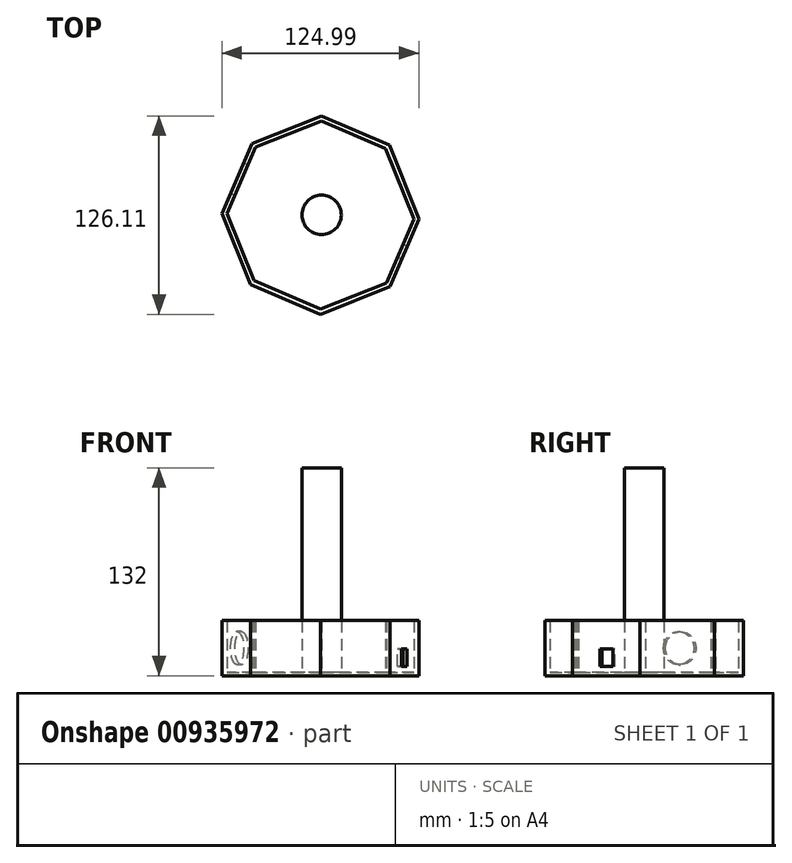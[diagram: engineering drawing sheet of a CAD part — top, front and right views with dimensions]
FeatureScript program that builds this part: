
annotation { "Feature Type Name" : "Feature", "Feature Type Description" : "" }
export const myFeature = defineFeature(function(context is Context, id is Id, definition is map)
    precondition{}
    {
        {
            var Q0;
            Q0=qCreatedBy(makeId("Top.planeOp"),FACE);
            var sketch = newSketch(context, id + "F0", { "sketchPlane" : qUnion([Q0])});
            skCircle(sketch, "E0.cCircle", {"center": v(0, 0) * mm, "radius": 60 * mm, "construction": true});
            skLineSegment(sketch, "E1.0", {"start": v(-44.1, 45.28) * mm, "end": v(0.06, 62.9) * mm});
            skLineSegment(sketch, "E1.1", {"start": v(0.06, 62.9) * mm, "end": v(42.99, 44.45) * mm});
            skLineSegment(sketch, "E1.2", {"start": v(42.99, 44.45) * mm, "end": v(61.78, -2.66) * mm});
            skLineSegment(sketch, "E1.3", {"start": v(61.78, -2.66) * mm, "end": v(43.34, -45.59) * mm});
            skLineSegment(sketch, "E1.4", {"start": v(43.34, -45.59) * mm, "end": v(-0.83, -63.2) * mm});
            skLineSegment(sketch, "E1.5", {"start": v(-0.83, -63.2) * mm, "end": v(-45.28, -44.1) * mm});
            skLineSegment(sketch, "E1.6", {"start": v(-45.28, -44.1) * mm, "end": v(-63.2, 0.83) * mm});
            skLineSegment(sketch, "E1.7", {"start": v(-63.2, 0.83) * mm, "end": v(-44.1, 45.28) * mm});
            skPoint(sketch, "E1.0.midPoint", {"position": v(-21.64, 54.24) * mm});
            skLineSegment(sketch, "E2.0", {"start": v(-59.96, 0.79) * mm, "end": v(-41.84, 42.96) * mm});
            skLineSegment(sketch, "E2.1", {"start": v(-42.96, -41.84) * mm, "end": v(-59.96, 0.79) * mm});
            skLineSegment(sketch, "E2.2", {"start": v(-41.84, 42.96) * mm, "end": v(0.02, 59.65) * mm});
            skLineSegment(sketch, "E2.3", {"start": v(-0.79, -59.96) * mm, "end": v(-42.96, -41.84) * mm});
            skLineSegment(sketch, "E2.4", {"start": v(0.02, 59.65) * mm, "end": v(40.66, 42.19) * mm});
            skLineSegment(sketch, "E2.5", {"start": v(40.66, 42.19) * mm, "end": v(58.54, -2.62) * mm});
            skLineSegment(sketch, "E2.6", {"start": v(58.54, -2.62) * mm, "end": v(41.07, -43.26) * mm});
            skLineSegment(sketch, "E2.7", {"start": v(41.07, -43.26) * mm, "end": v(-0.79, -59.96) * mm});
            skSolve(sketch);
        }
        {
            var Q0;
            Q0=makeQuery(id+"F0.imprint","IMPRINT",FACE,{"disambiguationData":[TD([[makeQuery(id+"F0.imprint","IMPRINT",EDGE,{"derivedFrom":sQuery(id+"F0.wireOp",EDGE,"E1.0")}),-1.0]])]});
            extrude(context, id + "F1", {"entities" : qUnion([Q0]), "depth" : 35 * mm, "offsetDistance" : 25 * mm});
        }
        {
            var Q0;
            Q0=makeQuery(id+"F0.imprint","IMPRINT",FACE,{"disambiguationData":[TD([[makeQuery(id+"F0.imprint","IMPRINT",EDGE,{"derivedFrom":sQuery(id+"F0.wireOp",EDGE,"E2.0")}),-1.0]])]});
            extrude(context, id + "F2", {"entities" : qUnion([Q0]), "operationType" : NewBodyOperationType.ADD, "depth" : 2 * mm, "offsetDistance" : 25 * mm});
        }
        {
            var Q0;
            Q0=makeQuery(id+"F1.opExtrude","SWEPT_FACE",FACE,{"disambiguationData":[OSD([sQuery(id+"F0.wireOp",EDGE,"E1.3")])]});
            var sketch = newSketch(context, id + "F3", { "sketchPlane" : qUnion([Q0])});
            skLineSegment(sketch, "E3.0.0", {"start": v(-24.78, 0) * mm, "end": v(21.95, 0) * mm});
            skLineSegment(sketch, "E3.0.1", {"start": v(21.95, 0) * mm, "end": v(21.95, 35) * mm});
            skLineSegment(sketch, "E3.0.2", {"start": v(21.95, 35) * mm, "end": v(-24.78, 35) * mm});
            skLineSegment(sketch, "E3.0.3", {"start": v(-24.78, 35) * mm, "end": v(-24.78, 0) * mm});
            skLineSegment(sketch, "E4", {"start": v(-24.78, 35) * mm, "end": v(21.95, 0) * mm, "construction": true});
            skLineSegment(sketch, "E5.bottom", {"start": v(-5.76, 17) * mm, "end": v(3.24, 17) * mm});
            skLineSegment(sketch, "E5.top", {"start": v(-5.76, 6) * mm, "end": v(3.24, 6) * mm});
            skLineSegment(sketch, "E5.left", {"start": v(-5.76, 17) * mm, "end": v(-5.76, 6) * mm});
            skLineSegment(sketch, "E5.right", {"start": v(3.24, 17) * mm, "end": v(3.24, 6) * mm});
            skPoint(sketch, "E5.middle", {"position": v(-1.41, 17.5) * mm});
            skLineSegment(sketch, "E6", {"start": v(-1.41, 35) * mm, "end": v(-1.41, 0) * mm, "construction": true});
            skSolve(sketch);
        }
        {
            var Q0;
            Q0=makeQuery(id+"F3.imprint","IMPRINT",FACE,{"disambiguationData":[TD([[makeQuery(id+"F3.imprint","IMPRINT",EDGE,{"derivedFrom":sQuery(id+"F3.wireOp",EDGE,"E5.bottom")}),-1.0]])]});
            var Q1;
            Q1=makeQuery(id+"F1.opExtrude","SWEPT_FACE",FACE,{"disambiguationData":[OSD([sQuery(id+"F0.wireOp",EDGE,"E2.6")])]});
            extrude(context, id + "F4", {"entities" : qUnion([Q0]), "operationType" : NewBodyOperationType.REMOVE, "endBound" : BoundingType.UP_TO_SURFACE, "oppositeDirection" : true, "depth" : 5 * mm, "endBoundEntityFace" : qUnion([Q1]), "offsetDistance" : 25 * mm});
        }
        {
            var Q0;
            Q0=makeQuery(id+"F2.opExtrude","CAP_FACE",FACE,{"disambiguationData":[OSD([sQuery(id+"F0.wireOp",EDGE,"E2.0"),sQuery(id+"F0.wireOp",EDGE,"E2.1"),sQuery(id+"F0.wireOp",EDGE,"E2.2"),sQuery(id+"F0.wireOp",EDGE,"E2.3"),sQuery(id+"F0.wireOp",EDGE,"E2.4"),sQuery(id+"F0.wireOp",EDGE,"E2.5"),sQuery(id+"F0.wireOp",EDGE,"E2.6"),sQuery(id+"F0.wireOp",EDGE,"E2.7")])],"isStart":false});
            var sketch = newSketch(context, id + "F5", { "sketchPlane" : qUnion([Q0])});
            skCircle(sketch, "E7", {"center": v(0, 0) * mm, "radius": 12.5 * mm});
            skSolve(sketch);
        }
        {
            var Q0;
            Q0=makeQuery(id+"F5.imprint","IMPRINT",FACE,{"disambiguationData":[TD([[makeQuery(id+"F5.imprint","IMPRINT",EDGE,{"derivedFrom":sQuery(id+"F5.wireOp",EDGE,"E7")}),1.0]])]});
            extrude(context, id + "F6", {"entities" : qUnion([Q0]), "operationType" : NewBodyOperationType.ADD, "depth" : 130 * mm, "offsetDistance" : 25 * mm});
        }
        {
            var Q0;
            Q0=makeQuery(id+"F1.opExtrude","SWEPT_FACE",FACE,{"disambiguationData":[OSD([sQuery(id+"F0.wireOp",EDGE,"E1.7")])]});
            var sketch = newSketch(context, id + "F7", { "sketchPlane" : qUnion([Q0])});
            skLineSegment(sketch, "E8", {"start": v(-24.2, 35) * mm, "end": v(24.2, 0) * mm, "construction": true});
            skCircle(sketch, "E9", {"center": v(0, 17.5) * mm, "radius": 10.5 * mm});
            skSolve(sketch);
        }
        {
            var Q0;
            Q0=makeQuery(id+"F7.imprint","IMPRINT",FACE,{"disambiguationData":[TD([[makeQuery(id+"F7.imprint","IMPRINT",EDGE,{"derivedFrom":sQuery(id+"F7.wireOp",EDGE,"E9")}),1.0]])]});
            var Q1;
            Q1=makeQuery(id+"F1.opExtrude","SWEPT_FACE",FACE,{"disambiguationData":[OSD([sQuery(id+"F0.wireOp",EDGE,"E2.0")])]});
            extrude(context, id + "F8", {"entities" : qUnion([Q0]), "operationType" : NewBodyOperationType.REMOVE, "endBound" : BoundingType.UP_TO_SURFACE, "oppositeDirection" : true, "depth" : 25 * mm, "endBoundEntityFace" : qUnion([Q1]), "offsetDistance" : 25 * mm});
        }
    });
